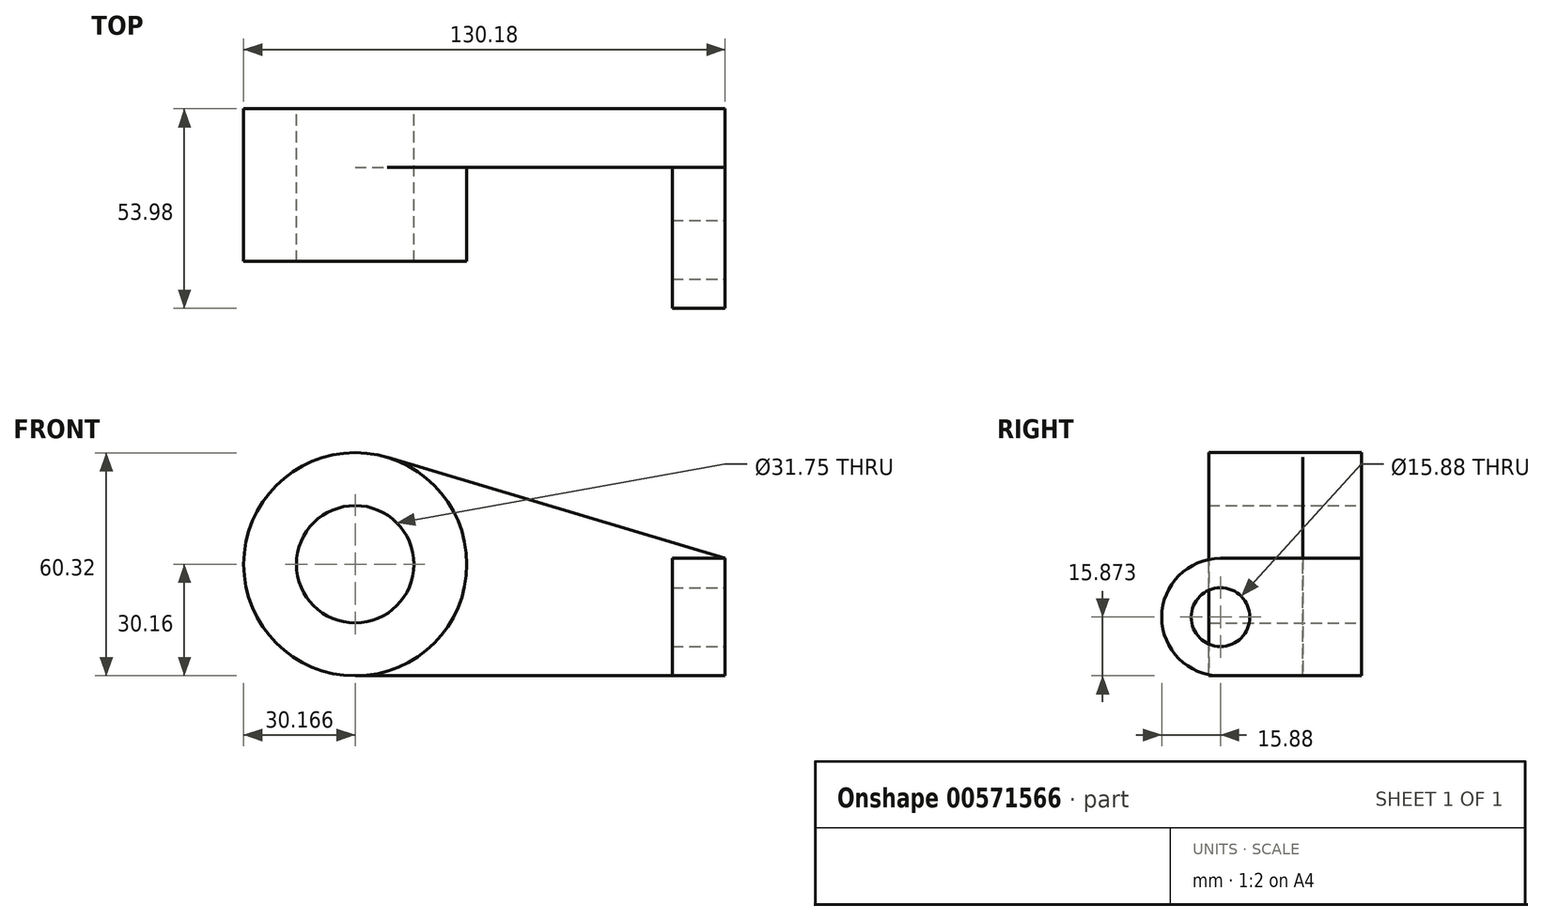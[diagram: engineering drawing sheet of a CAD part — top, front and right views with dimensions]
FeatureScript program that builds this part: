
annotation { "Feature Type Name" : "Feature", "Feature Type Description" : "" }
export const myFeature = defineFeature(function(context is Context, id is Id, definition is map)
    precondition{}
    {
        {
            var Q0;
            Q0=qCreatedBy(makeId("Front.planeOp"),FACE);
            var sketch = newSketch(context, id + "F0", { "sketchPlane" : qUnion([Q0])});
            skCircle(sketch, "E0", {"center": v(-43.27, 0) * mm, "radius": 30.16 * mm});
            skCircle(sketch, "E1", {"center": v(-43.27, 0) * mm, "radius": 15.88 * mm});
            skSolve(sketch);
        }
        {
            var Q0;
            Q0 = qSketchRegion(id + "F0", true);
            extrude(context, id + "F1", {"entities" : qUnion([Q0]), "depth" : 41.27 * mm, "offsetDistance" : 25.4 * mm});
        }
        {
            var Q0;
            Q0=makeQuery(id+"F1.opExtrude","CAP_FACE",FACE,{"disambiguationData":[OSD([sQuery(id+"F0.wireOp",EDGE,"E0"),sQuery(id+"F0.wireOp",EDGE,"E1")])],"isStart":true});
            var sketch = newSketch(context, id + "F2", { "sketchPlane" : qUnion([Q0])});
            skLineSegment(sketch, "E2", {"start": v(43.27, -30.16) * mm, "end": v(-56.74, -30.16) * mm});
            skLineSegment(sketch, "E3", {"start": v(-56.74, -30.16) * mm, "end": v(-56.74, 1.59) * mm});
            skLineSegment(sketch, "E4", {"start": v(-56.74, 1.59) * mm, "end": v(34.64, 28.9) * mm});
            skPoint(sketch, "E5.start.orphan", {"position": v(43.27, 0) * mm});
            skLineSegment(sketch, "E6", {"start": v(34.64, 28.9) * mm, "end": v(43.27, -30.16) * mm});
            skSolve(sketch);
        }
        {
            var Q0;
            {var subQ0=sQuery(id+"F2.wireOp",EDGE,"E2");Q0=makeQuery(id+"F2.imprint","IMPRINT",FACE,{"disambiguationData":[TD([[makeQuery(id+"F2.imprint","IMPRINT",EDGE,{"derivedFrom":subQ0}),-1.0]])]});}
            extrude(context, id + "F3", {"entities" : qUnion([Q0]), "operationType" : NewBodyOperationType.ADD, "oppositeDirection" : true, "depth" : 15.88 * mm, "offsetDistance" : 25.4 * mm});
        }
        {
            var Q0;
            Q0=makeQuery(id+"F3.opExtrude","CAP_FACE",FACE,{"disambiguationData":[OSD([sQuery(id+"F0.wireOp",EDGE,"E0"),sQuery(id+"F2.wireOp",EDGE,"E2"),sQuery(id+"F2.wireOp",EDGE,"E3"),sQuery(id+"F2.wireOp",EDGE,"E4")])],"isStart":false});
            var sketch = newSketch(context, id + "F4", { "sketchPlane" : qUnion([Q0])});
            skLineSegment(sketch, "E7.bottom", {"start": v(56.74, 1.59) * mm, "end": v(42.45, 1.59) * mm});
            skLineSegment(sketch, "E7.top", {"start": v(56.74, -30.16) * mm, "end": v(42.45, -30.16) * mm});
            skLineSegment(sketch, "E7.left", {"start": v(56.74, 1.59) * mm, "end": v(56.74, -30.16) * mm});
            skLineSegment(sketch, "E7.right", {"start": v(42.45, 1.59) * mm, "end": v(42.45, -30.16) * mm});
            skSolve(sketch);
        }
        {
            var Q0;
            Q0 = qSketchRegion(id + "F4", true);
            extrude(context, id + "F5", {"entities" : qUnion([Q0]), "operationType" : NewBodyOperationType.ADD, "depth" : 22.22 * mm, "offsetDistance" : 25.4 * mm});
        }
        {
            var Q0;
            Q0=makeQuery(id+"F5.boolean.opBoolean","MERGE",FACE,{"derivedFrom":[makeQuery(id+"F3.opExtrude","SWEPT_FACE",FACE,{"disambiguationData":[OSD([sQuery(id+"F2.wireOp",EDGE,"E3")])]}),makeQuery(id+"F5.opExtrude","SWEPT_FACE",FACE,{"disambiguationData":[OSD([sQuery(id+"F4.wireOp",EDGE,"E7.left")])]})]});
            var sketch = newSketch(context, id + "F6", { "sketchPlane" : qUnion([Q0])});
            skArc(sketch, "E8", {"start": v(-38.1, 1.59) * mm, "mid": v(-53.98, -14.29) * mm, "end": v(-38.1, -30.16) * mm});
            skSolve(sketch);
        }
        {
            var Q0;
            Q0=makeQuery(id+"F6.imprint","IMPRINT",FACE,{"disambiguationData":[TD([[makeQuery(id+"F6.imprint","IMPRINT",EDGE,{"derivedFrom":sQuery(id+"F6.wireOp",EDGE,"E8")}),1.0]])]});
            extrude(context, id + "F7", {"entities" : qUnion([Q0]), "operationType" : NewBodyOperationType.ADD, "oppositeDirection" : true, "depth" : 14.29 * mm, "offsetDistance" : 25.4 * mm});
        }
        {
            var Q0;
            {var subQ0=sQuery(id+"F4.wireOp",EDGE,"E7.left");Q0=makeQuery(id+"F7.boolean.opBoolean","MERGE",FACE,{"derivedFrom":[makeQuery(id+"F5.boolean.opBoolean","MERGE",FACE,{"derivedFrom":[makeQuery(id+"F3.opExtrude","SWEPT_FACE",FACE,{"disambiguationData":[OSD([sQuery(id+"F2.wireOp",EDGE,"E3")])]}),makeQuery(id+"F5.opExtrude","SWEPT_FACE",FACE,{"disambiguationData":[OSD([subQ0])]})]}),makeQuery(id+"F7.opExtrude","CAP_FACE",FACE,{"disambiguationData":[OSD([subQ0,sQuery(id+"F6.wireOp",EDGE,"E8")])],"isStart":true})]});}
            var sketch = newSketch(context, id + "F8", { "sketchPlane" : qUnion([Q0])});
            skCircle(sketch, "E9", {"center": v(-38.1, -14.29) * mm, "radius": 7.94 * mm});
            skSolve(sketch);
        }
        {
            var Q0;
            Q0=makeQuery(id+"F8.imprint","IMPRINT",FACE,{"disambiguationData":[TD([[makeQuery(id+"F8.imprint","IMPRINT",EDGE,{"derivedFrom":sQuery(id+"F8.wireOp",EDGE,"E9")}),1.0]])]});
            extrude(context, id + "F9", {"entities" : qUnion([Q0]), "operationType" : NewBodyOperationType.REMOVE, "oppositeDirection" : true, "depth" : 25.4 * mm, "offsetDistance" : 25.4 * mm});
        }
    });
